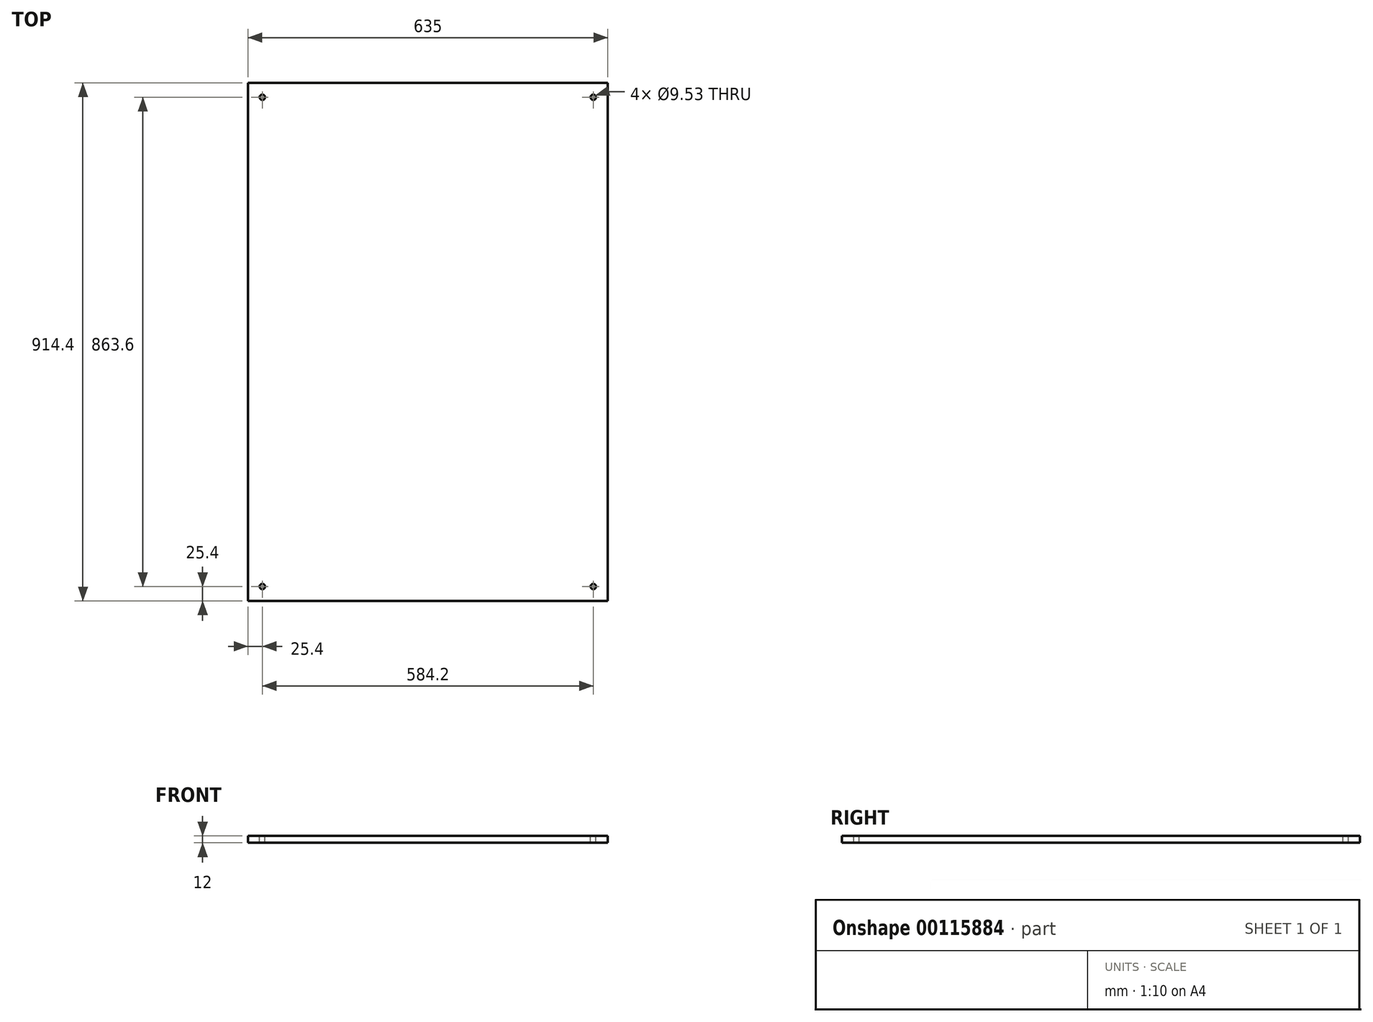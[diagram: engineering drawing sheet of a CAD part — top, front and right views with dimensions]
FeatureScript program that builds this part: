
annotation { "Feature Type Name" : "Feature", "Feature Type Description" : "" }
export const myFeature = defineFeature(function(context is Context, id is Id, definition is map)
    precondition{}
    {
        {
            var Q0;
            Q0=qCreatedBy(makeId("Top.planeOp"),FACE);
            var sketch = newSketch(context, id + "F0", { "sketchPlane" : qUnion([Q0])});
            skLineSegment(sketch, "E0.rect.bottom", {"start": v(305.5, -445.2) * mm, "end": v(-305.5, -445.2) * mm});
            skLineSegment(sketch, "E0.rect.top", {"start": v(305.5, 445.2) * mm, "end": v(-305.5, 445.2) * mm});
            skLineSegment(sketch, "E0.rect.left", {"start": v(305.5, -445.2) * mm, "end": v(305.5, 445.2) * mm});
            skLineSegment(sketch, "E0.rect.right", {"start": v(-305.5, -445.2) * mm, "end": v(-305.5, 445.2) * mm});
            skPoint(sketch, "E0.rect.middle", {"position": v(0, 0) * mm});
            skLineSegment(sketch, "E1.rect.bottom", {"start": v(317.5, -457.2) * mm, "end": v(-317.5, -457.2) * mm});
            skLineSegment(sketch, "E1.rect.top", {"start": v(317.5, 457.2) * mm, "end": v(-317.5, 457.2) * mm});
            skLineSegment(sketch, "E1.rect.left", {"start": v(317.5, -457.2) * mm, "end": v(317.5, 457.2) * mm});
            skLineSegment(sketch, "E1.rect.right", {"start": v(-317.5, -457.2) * mm, "end": v(-317.5, 457.2) * mm});
            skSolve(sketch);
        }
        {
            var Q0;
            Q0=qSketchRegion(id+"F0",true);
            var Q1;
            Q1=makeQuery(id+"F0.imprint","IMPRINT",FACE,{"disambiguationData":[TD([[makeQuery(id+"F0.imprint","IMPRINT",EDGE,{"derivedFrom":sQuery(id+"F0.wireOp",EDGE,"E0.rect.bottom")}),-1.0]])]});
            extrude(context, id + "F1", {"entities" : qUnion([Q0, Q1]), "endBound" : BoundingType.SYMMETRIC, "oppositeDirection" : true, "depth" : 12 * mm});
        }
        {
            var Q0;
            Q0=makeQuery(id+"F1.opExtrude","CAP_FACE",FACE,{"disambiguationData":[OSD([sQuery(id+"F0.wireOp",EDGE,"E1.rect.bottom"),sQuery(id+"F0.wireOp",EDGE,"E1.rect.top"),sQuery(id+"F0.wireOp",EDGE,"E1.rect.left"),sQuery(id+"F0.wireOp",EDGE,"E1.rect.right")])],"isStart":true});
            var sketch = newSketch(context, id + "F2", { "sketchPlane" : qUnion([Q0])});
            skLineSegment(sketch, "E2.rect.bottom", {"start": v(-292.1, 431.8) * mm, "end": v(292.1, 431.8) * mm, "construction": true});
            skLineSegment(sketch, "E2.rect.top", {"start": v(-292.1, -431.8) * mm, "end": v(292.1, -431.8) * mm, "construction": true});
            skLineSegment(sketch, "E2.rect.left", {"start": v(-292.1, 431.8) * mm, "end": v(-292.1, -431.8) * mm, "construction": true});
            skLineSegment(sketch, "E2.rect.right", {"start": v(292.1, 431.8) * mm, "end": v(292.1, -431.8) * mm, "construction": true});
            skPoint(sketch, "E2.rect.middle", {"position": v(0, 0) * mm});
            skCircle(sketch, "E3", {"center": v(-292.1, 431.8) * mm, "radius": 4.76 * mm});
            skCircle(sketch, "E4", {"center": v(292.1, 431.8) * mm, "radius": 4.76 * mm});
            skCircle(sketch, "E5", {"center": v(-292.1, -431.8) * mm, "radius": 4.76 * mm});
            skCircle(sketch, "E6", {"center": v(292.1, -431.8) * mm, "radius": 4.76 * mm});
            skSolve(sketch);
        }
        {
            var Q0;
            Q0=qSketchRegion(id+"F2",true);
            extrude(context, id + "F3", {"entities" : qUnion([Q0]), "operationType" : NewBodyOperationType.REMOVE, "oppositeDirection" : true, "depth" : 25.4 * mm});
        }
    });
